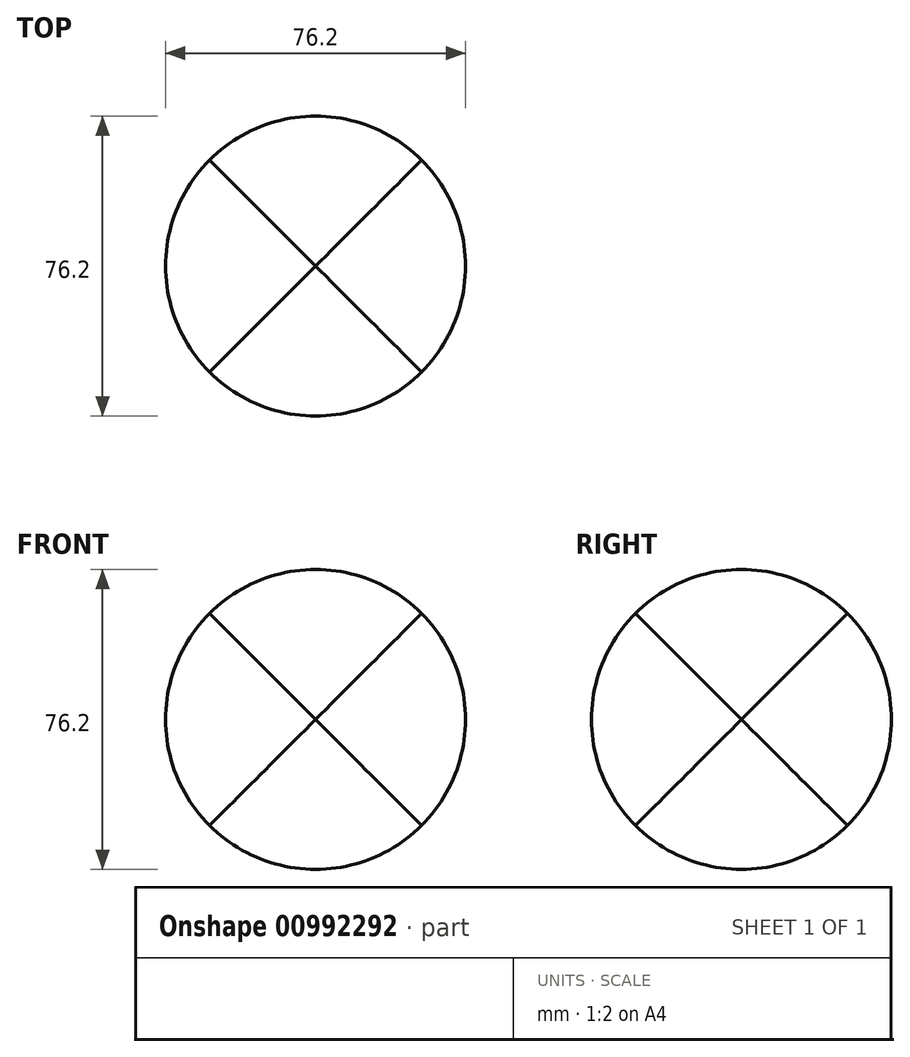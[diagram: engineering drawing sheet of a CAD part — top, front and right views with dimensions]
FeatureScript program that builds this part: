
annotation { "Feature Type Name" : "Feature", "Feature Type Description" : "" }
export const myFeature = defineFeature(function(context is Context, id is Id, definition is map)
    precondition{}
    {
        {
            var Q0;
            Q0=qCreatedBy(makeId("Front.planeOp"),FACE);
            var sketch = newSketch(context, id + "F0", { "sketchPlane" : qUnion([Q0])});
            skCircle(sketch, "E0", {"center": v(0, 0) * mm, "radius": 38.1 * mm});
            skSolve(sketch);
        }
        {
            var Q0;
            Q0=makeQuery(id+"F0.imprint","IMPRINT",FACE,{"disambiguationData":[TD([[makeQuery(id+"F0.imprint","IMPRINT",EDGE,{"derivedFrom":sQuery(id+"F0.wireOp",EDGE,"E0")}),1.0]])]});
            extrude(context, id + "F1", {"entities" : qUnion([Q0]), "endBound" : BoundingType.SYMMETRIC, "depth" : 76.2 * mm, "offsetDistance" : 25.4 * mm});
        }
        {
            var Q0;
            Q0=qCreatedBy(makeId("Top.planeOp"),FACE);
            var sketch = newSketch(context, id + "F2", { "sketchPlane" : qUnion([Q0])});
            skCircle(sketch, "E1", {"center": v(0, 0) * mm, "radius": 38.1 * mm});
            skSolve(sketch);
        }
        {
            var Q0;
            Q0 = qSketchRegion(id + "F2", true);
            var Q1;
            Q1=sQuery(id+"F2.wireOp",EDGE,"E1");
            extrude(context, id + "F3", {"entities" : qUnion([Q0]), "operationType" : NewBodyOperationType.INTERSECT, "surfaceEntities" : qUnion([Q1]), "endBound" : BoundingType.SYMMETRIC, "depth" : 89.4 * mm, "offsetDistance" : 25.4 * mm});
        }
        {
            var Q0;
            Q0=qCreatedBy(makeId("Right.planeOp"),FACE);
            var sketch = newSketch(context, id + "F4", { "sketchPlane" : qUnion([Q0])});
            skCircle(sketch, "E2", {"center": v(0, 0) * mm, "radius": 38.1 * mm});
            skSolve(sketch);
        }
        {
            var Q0;
            Q0 = qSketchRegion(id + "F4", true);
            extrude(context, id + "F5", {"entities" : qUnion([Q0]), "operationType" : NewBodyOperationType.INTERSECT, "endBound" : BoundingType.SYMMETRIC, "depth" : 126.5 * mm, "offsetDistance" : 25.4 * mm});
        }
    });
